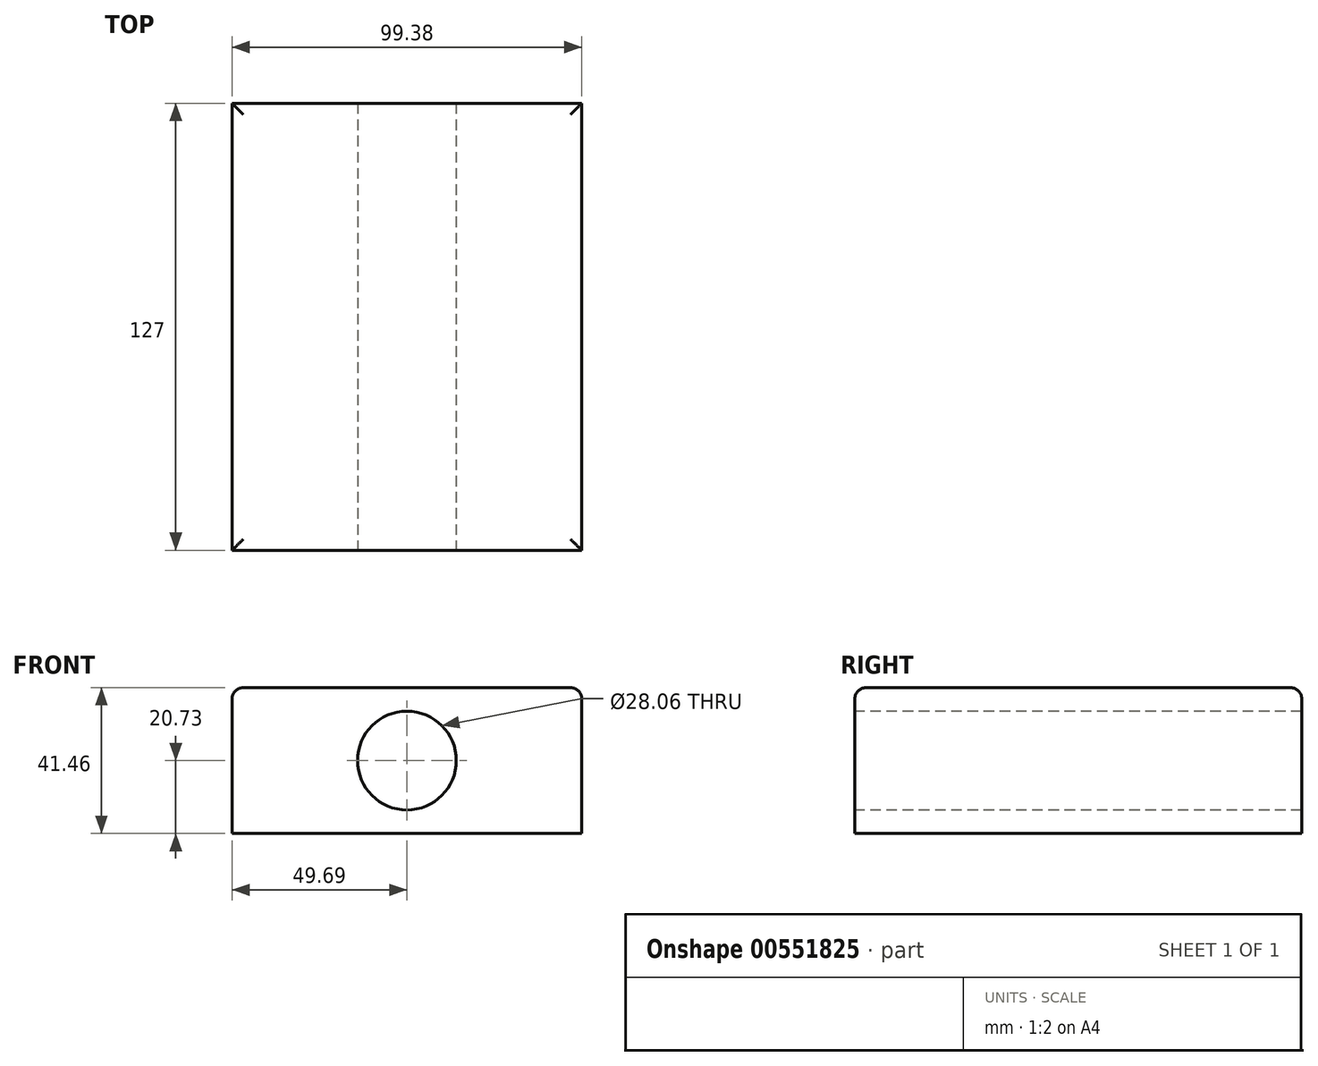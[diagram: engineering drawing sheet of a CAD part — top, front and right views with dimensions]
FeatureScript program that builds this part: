
annotation { "Feature Type Name" : "Feature", "Feature Type Description" : "" }
export const myFeature = defineFeature(function(context is Context, id is Id, definition is map)
    precondition{}
    {
        {
            var Q0;
            Q0=qCreatedBy(makeId("Front.planeOp"),FACE);
            var sketch = newSketch(context, id + "F0", { "sketchPlane" : qUnion([Q0])});
            skLineSegment(sketch, "E0.bottom", {"start": v(-49.69, 20.73) * mm, "end": v(49.69, 20.73) * mm});
            skLineSegment(sketch, "E0.top", {"start": v(-49.69, -20.73) * mm, "end": v(49.69, -20.73) * mm});
            skLineSegment(sketch, "E0.left", {"start": v(-49.69, 20.73) * mm, "end": v(-49.69, -20.73) * mm});
            skLineSegment(sketch, "E0.right", {"start": v(49.69, 20.73) * mm, "end": v(49.69, -20.73) * mm});
            skPoint(sketch, "E0.middle", {"position": v(0, 0) * mm});
            skSolve(sketch);
        }
        {
            var Q0;
            Q0=makeQuery(id+"F0.imprint","IMPRINT",FACE,{"disambiguationData":[TD([[makeQuery(id+"F0.imprint","IMPRINT",EDGE,{"derivedFrom":sQuery(id+"F0.wireOp",EDGE,"E0.bottom")}),-1.0]])]});
            extrude(context, id + "F1", {"entities" : qUnion([Q0]), "oppositeDirection" : true, "depth" : 127 * mm, "offsetDistance" : 25.4 * mm});
        }
        {
            var Q0;
            Q0=makeQuery(id+"F1.opExtrude","CAP_FACE",FACE,{"disambiguationData":[OSD([sQuery(id+"F0.wireOp",EDGE,"E0.bottom"),sQuery(id+"F0.wireOp",EDGE,"E0.top"),sQuery(id+"F0.wireOp",EDGE,"E0.left"),sQuery(id+"F0.wireOp",EDGE,"E0.right")])],"isStart":true});
            var sketch = newSketch(context, id + "F2", { "sketchPlane" : qUnion([Q0])});
            skCircle(sketch, "E1", {"center": v(0, 0) * mm, "radius": 14.03 * mm});
            skSolve(sketch);
        }
        {
            var Q0;
            Q0=makeQuery(id+"F2.imprint","IMPRINT",FACE,{"disambiguationData":[TD([[makeQuery(id+"F2.imprint","IMPRINT",EDGE,{"derivedFrom":sQuery(id+"F2.wireOp",EDGE,"E1")}),1.0]])]});
            extrude(context, id + "F3", {"entities" : qUnion([Q0]), "operationType" : NewBodyOperationType.REMOVE, "endBound" : BoundingType.THROUGH_ALL, "oppositeDirection" : true, "depth" : 25.4 * mm, "offsetDistance" : 25.4 * mm});
        }
        {
            var Q0;
            Q0=makeQuery(id+"F1.opExtrude","SWEPT_FACE",FACE,{"disambiguationData":[OSD([sQuery(id+"F0.wireOp",EDGE,"E0.bottom")])]});
            fillet(context, id + "F4", {"entities" : qUnion([Q0]), "radius" : 3.17 * mm, "tangentPropagation" : true, "allowEdgeOverflow" : false});
        }
    });
